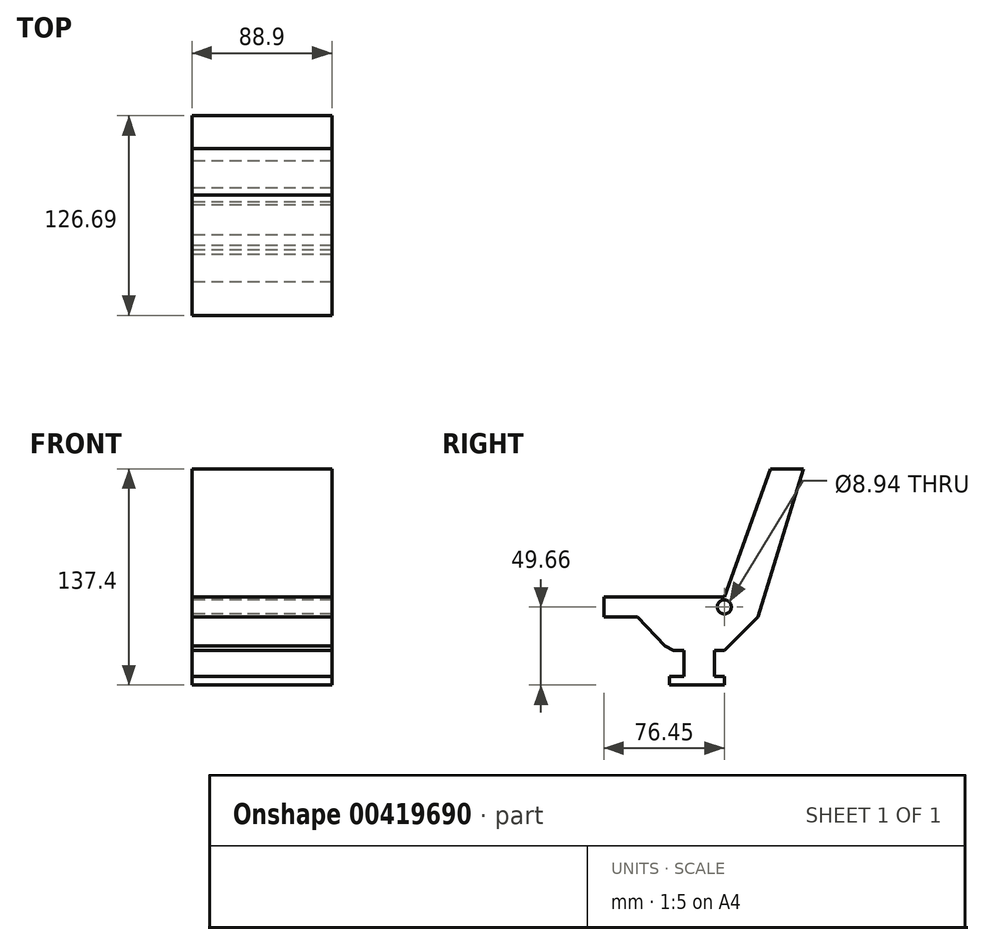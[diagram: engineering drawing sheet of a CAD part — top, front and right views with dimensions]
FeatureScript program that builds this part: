
annotation { "Feature Type Name" : "Feature", "Feature Type Description" : "" }
export const myFeature = defineFeature(function(context is Context, id is Id, definition is map)
    precondition{}
    {
        {
            var Q0;
            Q0=qCreatedBy(makeId("Right.planeOp"),FACE);
            var sketch = newSketch(context, id + "F0", { "sketchPlane" : qUnion([Q0])});
            skCircle(sketch, "E0", {"center": v(0, 0) * mm, "radius": 4.47 * mm});
            skLineSegment(sketch, "E1.bottom", {"start": v(0, 0) * mm, "end": v(-76.45, 0) * mm});
            skLineSegment(sketch, "E1.top", {"start": v(0, 6.37) * mm, "end": v(-76.45, 6.37) * mm});
            skLineSegment(sketch, "E1.left", {"start": v(0, 0) * mm, "end": v(0, 6.37) * mm});
            skLineSegment(sketch, "E1.right", {"start": v(-76.45, 0) * mm, "end": v(-76.45, 6.37) * mm});
            skLineSegment(sketch, "E2.MirrorCS", {"start": v(-76.45, 0) * mm, "end": v(-76.45, -6.37) * mm});
            skLineSegment(sketch, "E3.MirrorCS", {"start": v(0, -6.37) * mm, "end": v(-76.45, -6.37) * mm});
            skLineSegment(sketch, "E4.MirrorCS", {"start": v(0, 0) * mm, "end": v(0, -6.37) * mm});
            skLineSegment(sketch, "E5", {"start": v(-55.28, -6.37) * mm, "end": v(-37.85, -24.92) * mm});
            skLineSegment(sketch, "E6", {"start": v(-37.85, -24.92) * mm, "end": v(-32.23, -27.73) * mm});
            skLineSegment(sketch, "E7", {"start": v(-32.23, -27.73) * mm, "end": v(0, -27.73) * mm});
            skLineSegment(sketch, "E8", {"start": v(0, -27.73) * mm, "end": v(0, -6.37) * mm});
            skLineSegment(sketch, "E9", {"start": v(0, -27.73) * mm, "end": v(21.4, -6.37) * mm});
            skLineSegment(sketch, "E10", {"start": v(21.4, -6.37) * mm, "end": v(50.24, 87.74) * mm});
            skLineSegment(sketch, "E11", {"start": v(21.4, -6.37) * mm, "end": v(0, -6.37) * mm});
            skLineSegment(sketch, "E12", {"start": v(50.24, 87.74) * mm, "end": v(29.3, 87.74) * mm});
            skLineSegment(sketch, "E13", {"start": v(29.3, 87.74) * mm, "end": v(0, 6.37) * mm});
            skLineSegment(sketch, "E14.bottom", {"start": v(-4.94, 6.37) * mm, "end": v(4.94, 6.37) * mm});
            skLineSegment(sketch, "E14.top", {"start": v(-4.94, -6.37) * mm, "end": v(4.94, -6.37) * mm});
            skLineSegment(sketch, "E15.bottom", {"start": v(-25.52, -27.73) * mm, "end": v(-6.37, -27.73) * mm});
            skLineSegment(sketch, "E15.top", {"start": v(-25.52, -44.22) * mm, "end": v(-6.37, -44.22) * mm});
            skLineSegment(sketch, "E15.left", {"start": v(-25.52, -27.73) * mm, "end": v(-25.52, -44.22) * mm});
            skLineSegment(sketch, "E15.right", {"start": v(-6.37, -27.73) * mm, "end": v(-6.37, -44.22) * mm});
            skLineSegment(sketch, "E16.bottom", {"start": v(-35, -44.22) * mm, "end": v(0, -44.22) * mm});
            skLineSegment(sketch, "E16.top", {"start": v(-35, -49.66) * mm, "end": v(0, -49.66) * mm});
            skLineSegment(sketch, "E16.left", {"start": v(-35, -44.22) * mm, "end": v(-35, -49.66) * mm});
            skLineSegment(sketch, "E16.right", {"start": v(0, -44.22) * mm, "end": v(0, -49.66) * mm});
            skSolve(sketch);
        }
        {
            var Q0;
            Q0 = qSketchRegion(id + "F0", true);
            extrude(context, id + "F1", {"entities" : qUnion([Q0]), "endBound" : BoundingType.SYMMETRIC, "depth" : 88.9 * mm});
        }
    });
